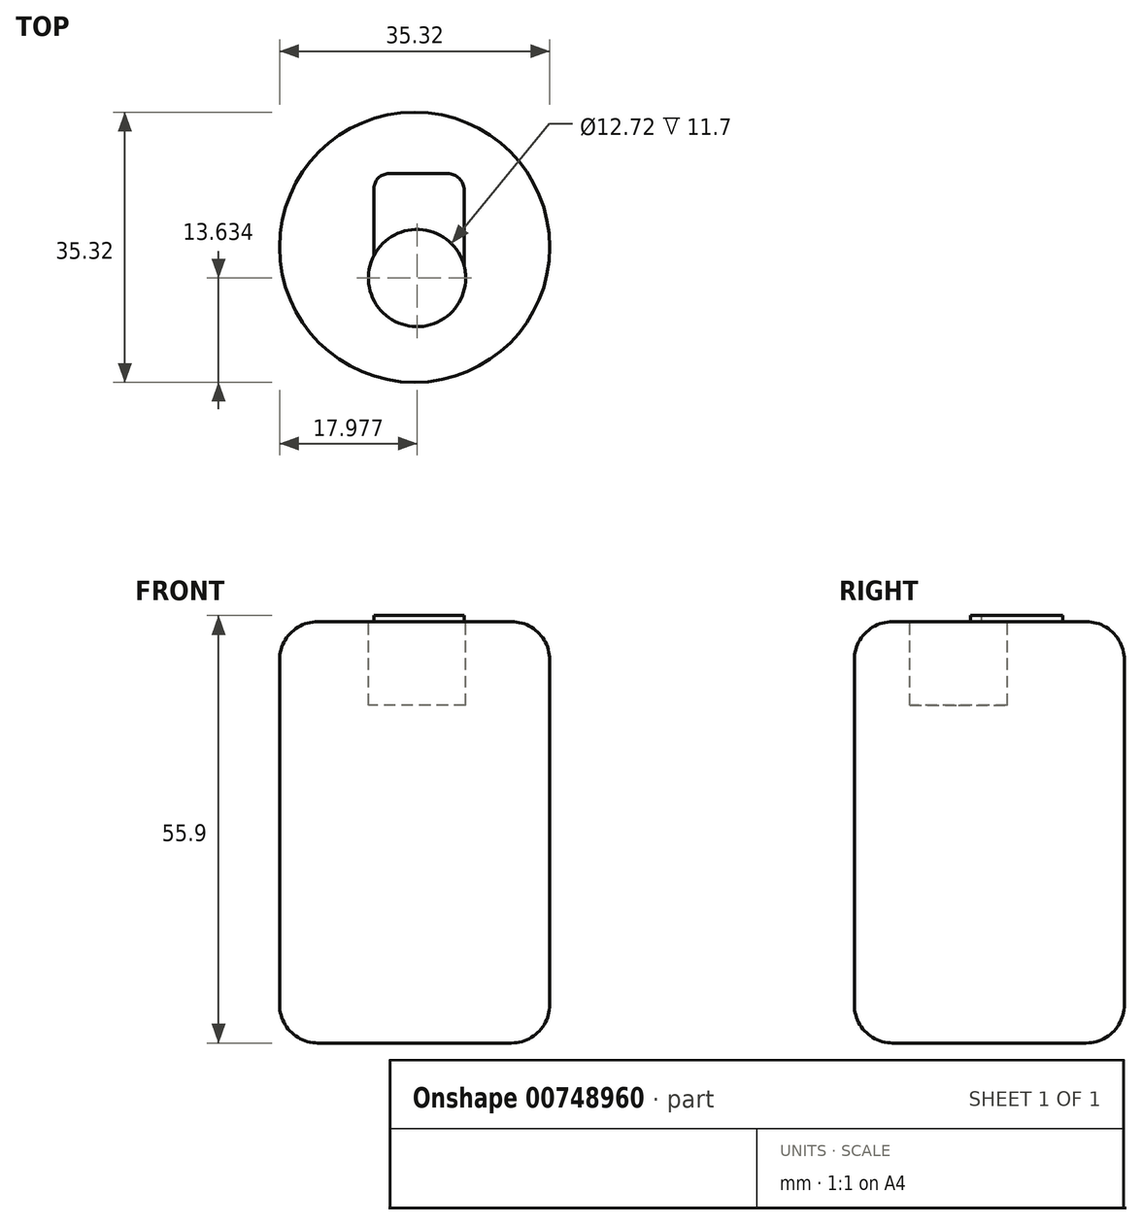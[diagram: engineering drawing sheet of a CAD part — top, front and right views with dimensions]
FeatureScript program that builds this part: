
annotation { "Feature Type Name" : "Feature", "Feature Type Description" : "" }
export const myFeature = defineFeature(function(context is Context, id is Id, definition is map)
    precondition{}
    {
        {
            var Q0;
            Q0=qCreatedBy(makeId("Top.planeOp"),FACE);
            var sketch = newSketch(context, id + "F0", { "sketchPlane" : qUnion([Q0])});
            skCircle(sketch, "E0", {"center": v(-60.17, 0) * mm, "radius": 17.66 * mm});
            skSolve(sketch);
        }
        {
            var Q0;
            Q0 = qSketchRegion(id + "F0", true);
            extrude(context, id + "F1", {"entities" : qUnion([Q0]), "depth" : 55.1 * mm, "offsetDistance" : 25 * mm});
        }
        {
            var Q0;
            Q0=makeQuery(id+"F1.opExtrude","CAP_EDGE",EDGE,{"disambiguationData":[OSD([sQuery(id+"F0.wireOp",EDGE,"E0")])],"isStart":true});
            var Q1;
            Q1=makeQuery(id+"F1.opExtrude","CAP_EDGE",EDGE,{"disambiguationData":[OSD([sQuery(id+"F0.wireOp",EDGE,"E0")])],"isStart":false});
            fillet(context, id + "F2", {"entities" : qUnion([Q0, Q1]), "radius" : 5 * mm, "tangentPropagation" : true, "allowEdgeOverflow" : false});
        }
        {
            var Q0;
            Q0=makeQuery(id+"F1.opExtrude","CAP_FACE",FACE,{"disambiguationData":[OSD([sQuery(id+"F0.wireOp",EDGE,"E0")])],"isStart":false});
            var sketch = newSketch(context, id + "F3", { "sketchPlane" : qUnion([Q0])});
            skCircle(sketch, "E1", {"center": v(-59.85, -4.03) * mm, "radius": 6.36 * mm});
            skSolve(sketch);
        }
        {
            var Q0;
            Q0=makeQuery(id+"F3.imprint","IMPRINT",FACE,{"disambiguationData":[TD([[makeQuery(id+"F3.imprint","IMPRINT",EDGE,{"derivedFrom":sQuery(id+"F3.wireOp",EDGE,"E1")}),1.0]])]});
            extrude(context, id + "F4", {"entities" : qUnion([Q0]), "operationType" : NewBodyOperationType.ADD, "depth" : 4.4 * mm, "offsetDistance" : 25 * mm});
        }
        {
            var Q0;
            Q0=makeQuery(id+"F4.opExtrude","CAP_FACE",FACE,{"disambiguationData":[OSD([sQuery(id+"F3.wireOp",EDGE,"E1")])],"isStart":false});
            extrude(context, id + "F5", {"entities" : qUnion([Q0]), "operationType" : NewBodyOperationType.REMOVE, "oppositeDirection" : true, "depth" : 9.1 * mm, "offsetDistance" : 25 * mm});
        }
        {
            var Q0;
            Q0=makeQuery(id+"F5.boolean.opBoolean","COPY",FACE,{"derivedFrom":makeQuery(id+"F5.opExtrude","CAP_FACE",FACE,{"disambiguationData":[OSD([sQuery(id+"F3.wireOp",EDGE,"E1")])],"isStart":false})});
            extrude(context, id + "F6", {"entities" : qUnion([Q0]), "operationType" : NewBodyOperationType.REMOVE, "oppositeDirection" : true, "depth" : 6.2 * mm, "offsetDistance" : 25 * mm});
        }
        {
            var Q0;
            Q0=makeQuery(id+"F1.opExtrude","CAP_FACE",FACE,{"disambiguationData":[OSD([sQuery(id+"F0.wireOp",EDGE,"E0")])],"isStart":false});
            var sketch = newSketch(context, id + "F7", { "sketchPlane" : qUnion([Q0])});
            skLineSegment(sketch, "E2.bottom", {"start": v(-65.48, 9.63) * mm, "end": v(-53.7, 9.63) * mm});
            skLineSegment(sketch, "E2.top", {"start": v(-65.48, -2.44) * mm, "end": v(-53.7, -2.44) * mm});
            skLineSegment(sketch, "E2.left", {"start": v(-65.48, 9.63) * mm, "end": v(-65.48, -2.44) * mm});
            skLineSegment(sketch, "E2.right", {"start": v(-53.7, 9.63) * mm, "end": v(-53.7, -2.44) * mm});
            skSolve(sketch);
        }
        {
            var Q0;
            {var subQ0=sQuery(id+"F7.wireOp",EDGE,"E2.bottom");Q0=makeQuery(id+"F7.imprint","IMPRINT",FACE,{"disambiguationData":[TD([[makeQuery(id+"F7.imprint","IMPRINT",EDGE,{"derivedFrom":subQ0}),-1.0]])]});}
            extrude(context, id + "F8", {"entities" : qUnion([Q0]), "operationType" : NewBodyOperationType.ADD, "depth" : 0.8 * mm, "offsetDistance" : 25 * mm});
        }
        {
            var Q0;
            Q0=makeQuery(id+"F8.opExtrude","SWEPT_EDGE",EDGE,{"disambiguationData":[OSD([sQuery(id+"F7.wireOp",EDGE,"E2.bottom"),sQuery(id+"F7.wireOp",EDGE,"E2.right")])]});
            fillet(context, id + "F9", {"entities" : qUnion([Q0]), "radius" : 2.17 * mm, "tangentPropagation" : true, "allowEdgeOverflow" : false});
        }
        {
            var Q0;
            Q0=makeQuery(id+"F8.opExtrude","SWEPT_EDGE",EDGE,{"disambiguationData":[OSD([sQuery(id+"F7.wireOp",EDGE,"E2.bottom"),sQuery(id+"F7.wireOp",EDGE,"E2.left")])]});
            fillet(context, id + "F10", {"entities" : qUnion([Q0]), "radius" : 1.93 * mm, "tangentPropagation" : true, "allowEdgeOverflow" : false});
        }
        {
            var Q0;
            Q0=makeQuery(id+"F8.opExtrude","CAP_FACE",FACE,{"disambiguationData":[OSD([sQuery(id+"F3.wireOp",EDGE,"E1"),sQuery(id+"F7.wireOp",EDGE,"E2.bottom"),sQuery(id+"F7.wireOp",EDGE,"E2.left"),sQuery(id+"F7.wireOp",EDGE,"E2.right")])],"isStart":false});
            var sketch = newSketch(context, id + "F11", { "sketchPlane" : qUnion([Q0])});
            skCircle(sketch, "E3", {"center": v(-59.7, 5.88) * mm, "radius": 2.8 * mm});
            skPoint(sketch, "E3.centerSnap0", {"position": v(-59.7, 9.63) * mm});
            skSolve(sketch);
        }
        {
            var Q0;
            Q0=sQuery(id+"F11.wireOp",EDGE,"E3");
            extrude(context, id + "F12", {"bodyType" : ToolBodyType.SURFACE, "surfaceEntities" : qUnion([Q0]), "oppositeDirection" : true, "depth" : 6.6 * mm, "offsetDistance" : 25 * mm});
        }
    });
